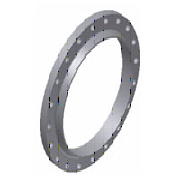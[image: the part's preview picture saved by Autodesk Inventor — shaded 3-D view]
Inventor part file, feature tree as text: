
AUTODESK INVENTOR PART (.ipt)
format: ipt  version: 2024.2 (Build 282272000, 272)  size: 260,608 bytes
history: native  units: mm
features: pattern_circular x1, sketch x1
ambient origin geometry x8: Origin, YZ Plane, XZ Plane, XY Plane, X Axis, Y Axis, Z Axis, Center Point
bodies: Solid1 (feature_tree)
feature tree (2):
  pattern_circular  "Circular Pattern1"  Count=59  [1 undecoded]
  sketch  "Sketch1"  dims[d1=450.0mm d2=522.0mm d3=514.0mm d4=5.0mm d7=35.0mm d8=45.0deg d9=65.0mm d10=3.0mm d14=3.217506mm d15=464.0mm d16=7.0mm d24=90.0deg d25=23.0mm d26=275.0mm d30=10.0mm d31=0.0mm d32=240.0mm d33=360.0deg]
note: 1 required parameter value undecoded (feature->parameter linkage not recoverable at this tier; creation-order binding heuristic only, values carry confidence <= 0.55)
